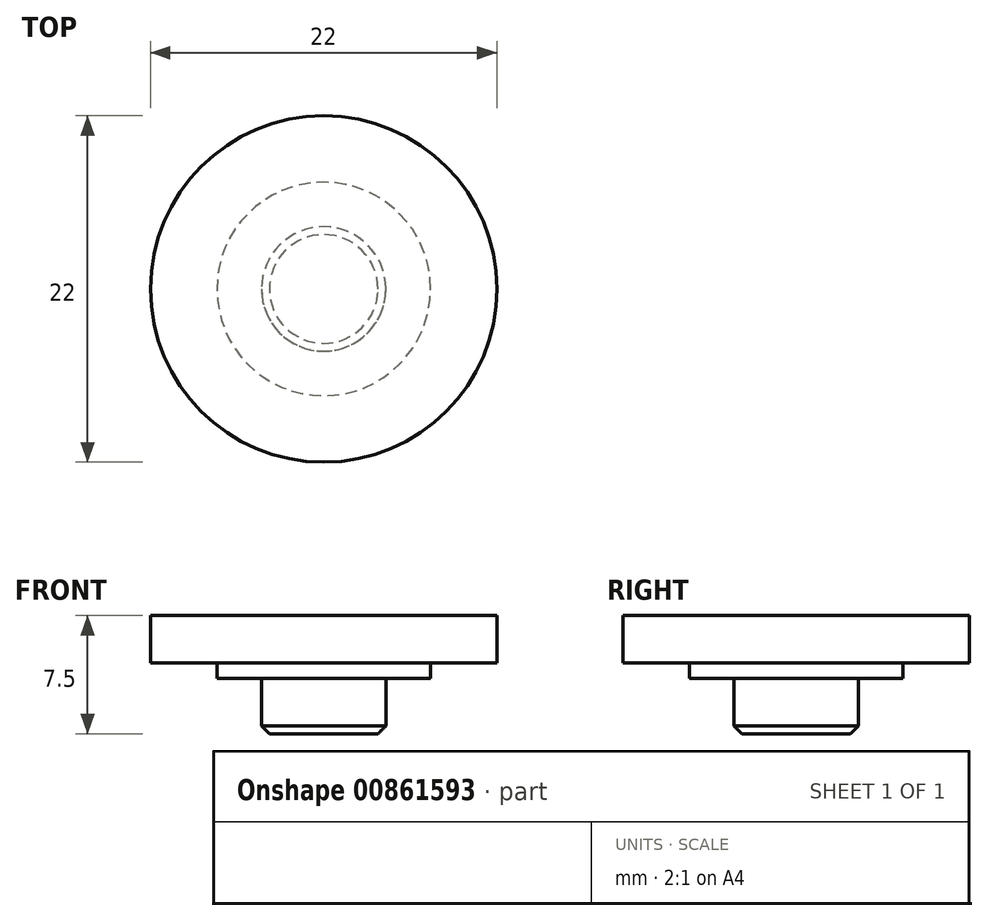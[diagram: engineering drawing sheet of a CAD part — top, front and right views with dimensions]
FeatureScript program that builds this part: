
annotation { "Feature Type Name" : "Feature", "Feature Type Description" : "" }
export const myFeature = defineFeature(function(context is Context, id is Id, definition is map)
    precondition{}
    {
        {
            var Q0;
            Q0=qCreatedBy(makeId("Front.planeOp"),FACE);
            var sketch = newSketch(context, id + "F0", { "sketchPlane" : qUnion([Q0])});
            skLineSegment(sketch, "E0", {"start": v(0, 7.5) * mm, "end": v(-11, 7.5) * mm});
            skLineSegment(sketch, "E1", {"start": v(-11, 7.5) * mm, "end": v(-11, 4.5) * mm});
            skLineSegment(sketch, "E2", {"start": v(-11, 4.5) * mm, "end": v(-6.78, 4.5) * mm});
            skLineSegment(sketch, "E3", {"start": v(-6.78, 4.5) * mm, "end": v(-6.78, 3.5) * mm});
            skLineSegment(sketch, "E4", {"start": v(-6.78, 3.5) * mm, "end": v(-3.95, 3.5) * mm});
            skLineSegment(sketch, "E5", {"start": v(-3.95, 3.5) * mm, "end": v(-3.95, 0) * mm});
            skLineSegment(sketch, "E6", {"start": v(-3.95, 0) * mm, "end": v(0, 0) * mm});
            skLineSegment(sketch, "E7", {"start": v(0, 0) * mm, "end": v(0, 7.5) * mm});
            skSolve(sketch);
        }
        {
            var Q0;
            Q0=makeQuery(id+"F0.imprint","IMPRINT",FACE,{"disambiguationData":[TD([[makeQuery(id+"F0.imprint","IMPRINT",EDGE,{"derivedFrom":sQuery(id+"F0.wireOp",EDGE,"E0")}),1.0]])]});
            var Q1;
            Q1=sQuery(id+"F0.wireOp",EDGE,"E7");
            revolve(context, id + "F1", {"surfaceOperationType" : NewSurfaceOperationType.NEW, "entities" : qUnion([Q0]), "axis" : qUnion([Q1]), "revolveType" : RevolveType.FULL});
        }
        {
            var Q0;
            Q0=makeQuery(id+"F1.opRevolve","SWEPT_FACE",FACE,{"disambiguationData":[OSD([sQuery(id+"F0.wireOp",EDGE,"E6")])]});
            chamfer(context, id + "F2", {"entities" : qUnion([Q0]), "width" : .5 * mm, "tangentPropagation" : true});
        }
    });
